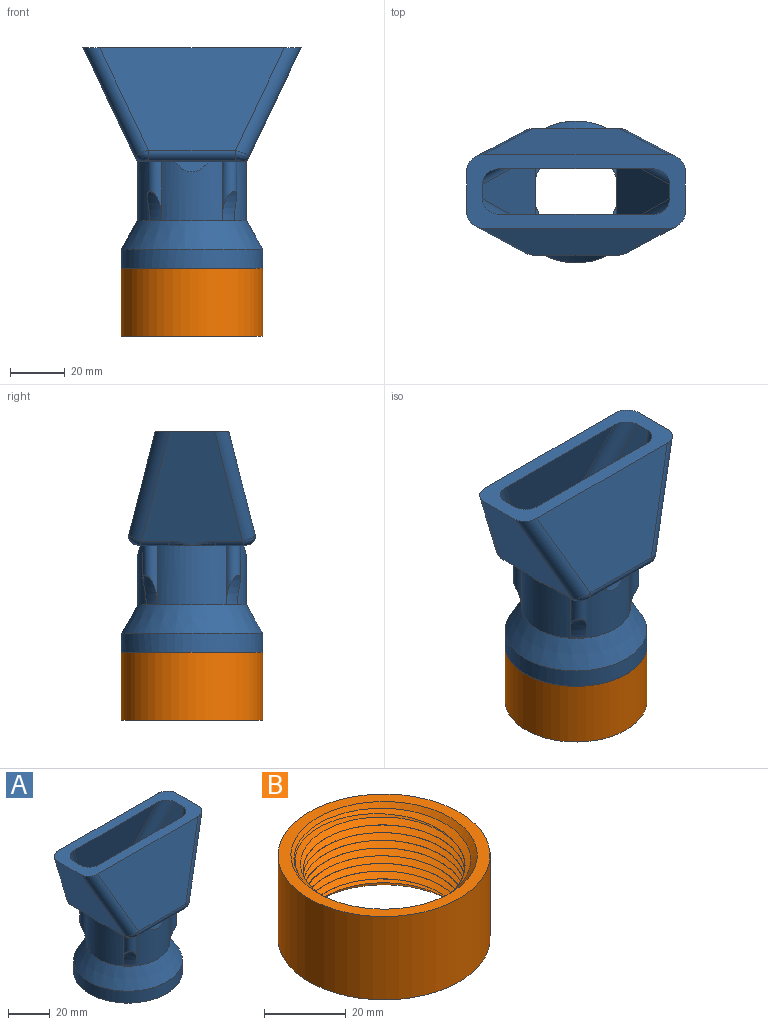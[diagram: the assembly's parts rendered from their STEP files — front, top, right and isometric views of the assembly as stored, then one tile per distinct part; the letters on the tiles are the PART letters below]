
ASSEMBLY  parts=2 mates=1
PART A: 75 faces, bbox 81.7x53.7x85.8 mm
  f0: cylinder r=20mm len=40mm, axis (0,0,1), area 2145.3mm2, adj f2,f3,f4,f7,f17,f23,f24,f33
  f1: plane 41.88x26.09mm, normal (0.91,0,0.42), area 734.3mm2, adj f10,f13,f20,f21,f41,f44,f46,f73
  f2: plane 11.98x10.55mm, normal (0,0,-1), area 30.8mm2, adj f0,f26,f48,f69,f70
  f3: plane 11.98x10.55mm, normal (0,0,-1), area 30.8mm2, adj f0,f27,f43,f61,f63
  f4: plane 11.98x10.55mm, normal (0,0,-1), area 30.8mm2, adj f0,f27,f38,f58,f60
  f5: plane 41.88x26.09mm, normal (-0.91,0,0.42), area 734.3mm2, adj f10,f19,f20,f21,f29,f31,f36,f71
  f6: plane 30.16x9.91mm, normal (0,-1,0), area 282.7mm2, adj f20,f28,f35,f37,f40,f42,f72,f73
  f7: plane 11.98x10.55mm, normal (0,0,-1), area 30.8mm2, adj f0,f26,f33,f65,f66
  f8: plane 67.79x37.64mm, normal (0,-0.97,0.25), area 1934mm2, adj f10,f49,f50,f68
  f9: plane 67.79x37.64mm, normal (0,0.97,0.25), area 1934mm2, adj f10,f51,f52,f62
  f10: plane 80.57x27.57mm, normal (0,0,1), area 1013.7mm2, adj f1,f5,f8,f9,f11,f12,f25,f28
  f11: plane 43.49x38.9mm, normal (0.9,0,-0.43), area 1208.4mm2, adj f10,f49,f52,f57,f58,f64,f65
  f12: plane 43.48x38.9mm, normal (-0.9,0,-0.43), area 1208.4mm2, adj f10,f50,f51,f59,f61,f67,f69
  f13: plane 9.6x0.75mm, normal (0,0,-1), area 4.8mm2, adj f1,f14
  f14: cylinder r=15.75mm len=35mm, axis (0,0,-1), area 3463.6mm2, adj f13,f18,f19,f20,f21
  f15: cylinder r=26mm len=52mm, axis (0,0,-1), area 1131.8mm2, adj f16,f17
  f16: plane 52x52mm, normal (0,0,-1), area 898.3mm2, adj f15,f18
  f17: cone r=20mm half-angle=30deg, axis (0,0,-1), area 1734.2mm2, adj f0,f15
  f18: cone r=19.75mm half-angle=45deg, axis (0,0,-1), area 630.9mm2, adj f14,f16
  f19: plane 9.6x0.75mm, normal (0,0,-1), area 4.8mm2, adj f5,f14
  f20: plane 30x11.7mm, normal (0,0,1), area 99.1mm2, adj f1,f5,f6,f14,f34,f37,f39,f42
  f21: plane 30x11.4mm, normal (0,0,1), area 92.2mm2, adj f1,f5,f14,f22,f30,f32,f45,f47
  f22: plane 31.24x11.08mm, normal (0,1,0), area 327.6mm2, adj f21,f25,f29,f32,f44,f47,f71,f74
  f23: plane 12.27x3.77mm, normal (0,-0.97,0.25), area 31.9mm2, adj f0,f26
  f24: plane 12.27x3.77mm, normal (0,0.97,0.25), area 31.9mm2, adj f0,f27
  f25: plane 56.58x30.71mm, normal (0,0.97,-0.25), area 1342.1mm2, adj f10,f22,f71,f74
  f26: plane 36.17x1.94mm, normal (0,-0.25,-0.97), area 70.4mm2, adj f2,f7,f23,f66,f68,f70
  f27: plane 36.17x1.94mm, normal (0,0.25,-0.97), area 70.4mm2, adj f3,f4,f24,f60,f62,f63
  f28: plane 56.58x31.88mm, normal (0,-0.97,-0.25), area 1375.4mm2, adj f6,f10,f72,f73
  f29: plane 4.17x4.16mm, normal (0,0,1), area 5.9mm2, adj f5,f22,f30,f31,f32,f71
  f30: plane 1.5x0.99mm, normal (-1,0,0), area 1.5mm2, adj f21,f29,f31,f32
  f31: cylinder r=3mm len=1.5mm, axis (0,0,1), area 0.7mm2, adj f5,f29,f30
  f32: cylinder r=20mm len=3.27mm, axis (0,0,1), area 6.6mm2, adj f21,f22,f29,f30
  f33: cylinder r=3mm len=21.5mm, axis (0,0,1), area 131.6mm2, adj f0,f7,f53
  f34: plane 1.5x0.69mm, normal (-1,0,0), area 1mm2, adj f20,f35,f36,f37
  f35: plane 4.58x4.16mm, normal (0,0,1), area 6.5mm2, adj f6,f34,f36,f37,f72
  f36: cylinder r=3mm len=1.5mm, axis (0,0,-1), area 0.7mm2, adj f5,f34,f35,f72
  f37: cylinder r=20mm len=3.7mm, axis (0,0,-1), area 7.4mm2, adj f6,f20,f34,f35
  f38: cylinder r=3mm len=21.5mm, axis (0,0,-1), area 131.6mm2, adj f0,f4,f54
  f39: plane 1.5x0.69mm, normal (1,0,0), area 1mm2, adj f20,f40,f41,f42
  f40: plane 4.58x4.16mm, normal (0,0,1), area 6.5mm2, adj f6,f39,f41,f42,f73
  f41: cylinder r=3mm len=1.5mm, axis (0,0,-1), area 0.7mm2, adj f1,f39,f40,f73
  f42: cylinder r=20mm len=3.7mm, axis (0,0,-1), area 7.4mm2, adj f6,f20,f39,f40
  f43: cylinder r=3mm len=21.5mm, axis (0,0,-1), area 131.6mm2, adj f0,f3,f55
  f44: plane 4.17x4.16mm, normal (0,0,1), area 5.9mm2, adj f1,f22,f45,f46,f47,f74
  f45: plane 1.5x0.99mm, normal (1,0,0), area 1.5mm2, adj f21,f44,f46,f47
  f46: cylinder r=3mm len=1.5mm, axis (0,0,-1), area 0.7mm2, adj f1,f44,f45
  f47: cylinder r=20mm len=3.27mm, axis (0,0,-1), area 6.6mm2, adj f21,f22,f44,f45
  f48: cylinder r=3mm len=21.5mm, axis (0,0,-1), area 131.6mm2, adj f0,f2,f56
  f49: cylinder r=5mm len=44.2mm, axis (-0.42,-0.22,-0.88), area 347.4mm2, adj f8,f10,f11,f65,f66
  f50: cylinder r=5mm len=44.2mm, axis (-0.42,0.22,0.88), area 347.4mm2, adj f8,f10,f12,f69,f70
  f51: cylinder r=5mm len=44.2mm, axis (0.42,0.22,-0.88), area 347.4mm2, adj f9,f10,f12,f61,f63
  f52: cylinder r=5mm len=44.2mm, axis (0.42,-0.22,0.88), area 347.4mm2, adj f9,f10,f11,f58,f60
  f53: torus R=40mm, axis (0,0,1), area 59.3mm2, adj f0,f33
  f54: torus R=40mm, axis (0,0,1), area 59.3mm2, adj f0,f38
  f55: torus R=40mm, axis (0,0,1), area 59.3mm2, adj f0,f43
  f56: torus R=40mm, axis (0,0,1), area 59.3mm2, adj f0,f48
  f57: bspline ~8.49x2.71mm, area 9.1mm2, adj f0,f11,f58
  f58: cylinder r=3mm len=10.55mm, axis (0,1,0), area 35.1mm2, adj f4,f11,f52,f57,f60
  f59: bspline ~8.49x2.71mm, area 9.1mm2, adj f0,f12,f61
  f60: bspline ~4.93x4.65mm, area 23.1mm2, adj f4,f27,f52,f58,f62
  f61: cylinder r=3mm len=10.55mm, axis (0,1,0), area 35.1mm2, adj f3,f12,f51,f59,f63
  f62: cylinder r=3mm len=31.76mm, axis (1,0,0), area 149.7mm2, adj f9,f27,f60,f63
  f63: bspline ~6.27x5.82mm, area 23.1mm2, adj f3,f27,f51,f61,f62
  f64: bspline ~8.49x2.71mm, area 9.1mm2, adj f0,f11,f65
  f65: cylinder r=3mm len=10.55mm, axis (0,1,0), area 35.1mm2, adj f7,f11,f49,f64,f66
  f66: bspline ~6.27x5.82mm, area 23.1mm2, adj f7,f26,f49,f65,f68
  f67: bspline ~8.49x2.71mm, area 9.1mm2, adj f0,f12,f69
  f68: cylinder r=3mm len=31.76mm, axis (-1,0,0), area 149.7mm2, adj f8,f26,f66,f70
  f69: cylinder r=3mm len=10.55mm, axis (0,1,0), area 35.1mm2, adj f2,f12,f50,f67,f70
  f70: bspline ~4.93x4.65mm, area 23.1mm2, adj f2,f26,f50,f68,f69
  f71: cylinder r=5mm len=44.7mm, axis (-0.41,-0.23,-0.88), area 344.6mm2, adj f5,f10,f22,f25,f29
  f72: cylinder r=5mm len=44.84mm, axis (-0.41,0.23,-0.88), area 352.5mm2, adj f5,f6,f10,f28,f35,f36
  f73: cylinder r=5mm len=44.84mm, axis (-0.41,-0.23,0.88), area 352.5mm2, adj f1,f6,f10,f28,f40,f41
  f74: cylinder r=5mm len=44.7mm, axis (-0.41,0.23,0.88), area 344.6mm2, adj f1,f10,f22,f25,f44
PART B: 10 faces, bbox 52x52x26.2 mm
  f0: cylinder r=19.85mm len=39.7mm, axis (0,0,-1), area 36.5mm2, adj f4,f7,f8,f9
  f1: cylinder r=26mm len=52mm, axis (0,0,-1), area 4084.1mm2, adj f2,f3
  f2: plane 52x52mm, normal (0,0,1), area 483.4mm2, adj f1,f6
  f3: plane 52x52mm, normal (0,0,-1), area 483.4mm2, adj f1,f5
  f4: cone r=22.85mm half-angle=45deg, axis (0,0,-1), area 0mm2, adj f0,f5,f8
  f5: cone r=22.85mm half-angle=45deg, axis (0,0,-1), area 359.8mm2, adj f3,f4,f8,f9
  f6: cone r=19.85mm half-angle=45deg, axis (0,0,1), area 358.9mm2, adj f2,f7,f8,f9
  f7: cone r=19.85mm half-angle=45deg, axis (0,0,1), area 0.9mm2, adj f0,f6,f8,f9
  f8: bspline ~50.38x48.07mm, area 3114.7mm2, adj f0,f4,f5,f6,f7,f9
  f9: bspline ~50.38x48.07mm, area 3128.7mm2, adj f0,f5,f6,f7,f8
PLACE A t=(-22.11,-5.65,-42.67)mm fixed
PLACE B t=(-22.11,-5.65,-67.67)mm
MATE fastened A.f15 <-> B.f1  axis (0,0,-1) through (-22.11,-5.65,-42.67)mm
